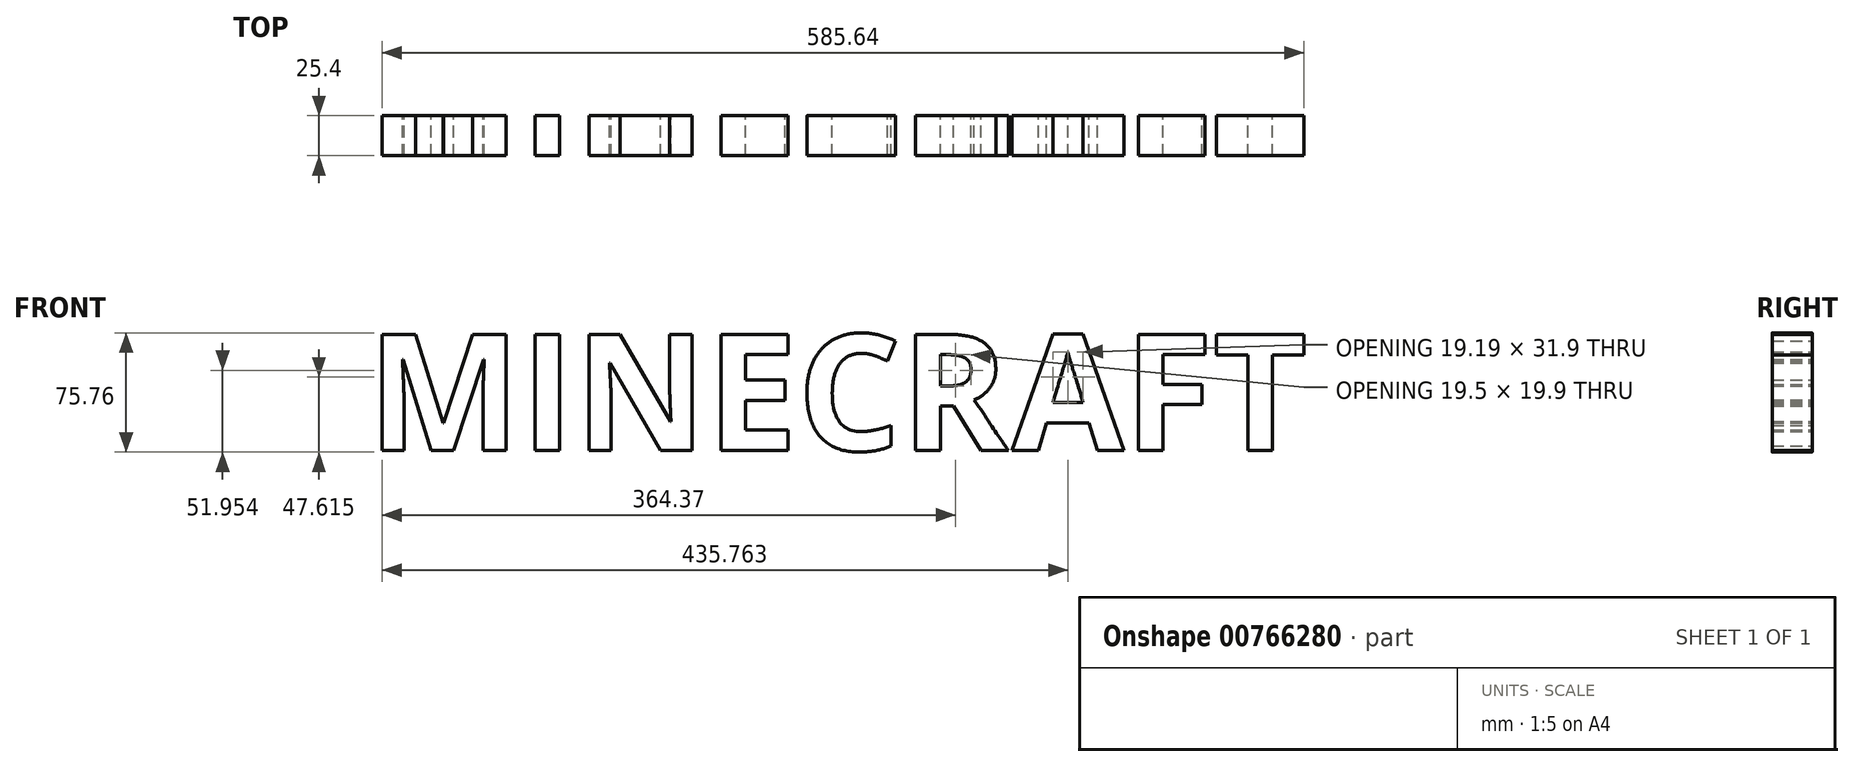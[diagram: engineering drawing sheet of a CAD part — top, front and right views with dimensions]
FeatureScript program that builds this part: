
annotation { "Feature Type Name" : "Feature", "Feature Type Description" : "" }
export const myFeature = defineFeature(function(context is Context, id is Id, definition is map)
    precondition{}
    {
        {
            var Q0;
            Q0=qCreatedBy(makeId("Front.planeOp"),FACE);
            var sketch = newSketch(context, id + "F0", { "sketchPlane" : qUnion([Q0])});
            skText(sketch, "E0", { "text": "MINECRAFT", "fontName": "OpenSans-Bold.ttf"});
            const initialGuessF0  = {"E0": [-0.06873, -0.02853, 1, 0, 0.07432]};
            skSetInitialGuess(sketch, initialGuessF0);
            skSolve(sketch);
        }
        {
            var Q0;
            Q0 = qSketchRegion(id + "F0", true);
            extrude(context, id + "F1", {"entities" : qUnion([Q0]), "depth" : 25.4 * mm, "offsetDistance" : 25.4 * mm});
        }
    });
